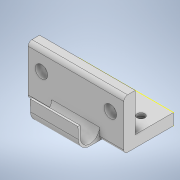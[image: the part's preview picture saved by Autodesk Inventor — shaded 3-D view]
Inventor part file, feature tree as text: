
AUTODESK INVENTOR PART (.ipt)
format: ipt  version: 2020 (Build 240168000, 168)  size: 232,448 bytes
history: native  units: in
note: dims shown in document units (in); Inventor stores cm internally (conversion verified against a paired STEP export)
features: sketch x7, extrude x4, plane x2, hole x2, direct_edit x1, mirror x1, fillet x1, move_body x1
ambient origin geometry x8: Origin, YZ Plane, XZ Plane, XY Plane, X Axis, Y Axis, Z Axis, Center Point
bodies: Solid1 (feature_tree)
feature tree (19):
  extrude  "Extrusion1"  Depth=1.0236in
  extrude  "Extrusion2"  Depth=0.7874in TaperAngle=0.0deg
  direct_edit  "Direct Edit1"
  extrude  "Extrusion7"  Depth=0.9843in
  plane  "Work Plane1"
  sketch  "Sketch8"  dims[d30=0.4724in d31=0.0in d45=0.3937in]
  hole  "Hole1"  [1 undecoded]
  hole  "Hole2"  [1 undecoded]
  sketch  "Sketch13"  dims[d85=0.6322in d90=0.4724in d92=0.4724in d95=0.2362in d96=0.2362in d97=0.2756in d98=0.3937in d99=0.1575in d100=0.2362in d101=0.2559in d102=0.1772in d103=90.0deg d104=0.315in d105=0.8108in d106=0.2362in d107=0.3937in d108=0.2756in d109=0.1575in d110=0.2362in d111=0.2559in d112=0.1772in d113=90.0deg d114=0.315in d115=0.8108in d116=90.0deg d117=0.4982in d118=0.0in d119=0.0787in d48=0.0197in d49=0.0344in d50=0.0197in d51=0.0344in d67=0.0197in d68=0.0344in d69=0.0197in d70=0.0344in d86=0.0197in d87=0.0344in d88=0.0197in d89=0.0344in]
  plane  "Work Plane3"
  mirror  "Mirror1"
  extrude  "Extrusion16"  Depth=0.2362in
  fillet  "Fillet4"  Radius=0.4724in
  sketch  "Sketch1"  dims[d0=0.9843in d1=1.0236in]
  sketch  "Sketch2"  dims[d2=0.2362in d3=0.0in d5=0.7874in d6=0.0in]
  sketch  "Sketch7"  dims[d16=0.0in d17=0.0in d18=0.9843in d29=0.9843in]
  sketch  "Sketch11"  dims[d79=0.4724in d80=0.3937in]
  sketch  "Sketch12"  dims[d81=0.1969in d82=0.2362in d83=0.4724in]
  move_body  "Move1"
note: 2 required parameter values undecoded (feature->parameter linkage not recoverable at this tier; creation-order binding heuristic only, values carry confidence <= 0.55)
